FREECAD ASSEMBLY — COMPONENT RECIPES ("LPHolderAssembly")

This assembly document has 2 components, labeled P0..P1 below (a component is one placed body or linked part). 1 of them carries a construction recipe — the FreeCAD feature program that regenerates the part from scratch, quoted from this document or its linked companion documents; the rest are supplied as boundary geometry only. No exploded tour is included for this assembly.
COMPONENT P0 — geometry summary ("Body001"; no construction recipe available for this part):
  bounding box: 159.3 x 92.6 x 7.3 mm
  tessellated surface: 30,212 triangles
  volume: 10545 mm^3 (10% of its bounding box)
  symmetry: mirror-symmetric across its y mid-plane
COMPONENT P1 — recipe-attached ("Record Case", a linked part whose construction recipe lives in a companion FreeCAD document of the same project; that document's serialized recipe follows).
Construction recipe (the companion document, serialized — sketch geometry with constraints, then the solid features built on it; lengths are millimeters unless a unit is written):

FCSTD DOCUMENT  (FreeCAD 1.2R20251216 (Git shallow))
Label: Record
License: All rights reserved
objects: Sketcher::SketchObject×2, PartDesign::Pad×2, App::Point×1, PartDesign::Body×1
note: 11 computed .brp shape members not serialized (recipe doc carries the construction recipe); baked Part::Feature solids carry a one-line shape summary decoded from their .brp

FEATURE [App::Point] Origin001
  Role = Origin
FEATURE [Sketcher::SketchObject] Sketch
  ArcFitTolerance = 1e-06
  AttachmentSupport = -> [Origin]
  ExternalTypes = [0]
  FullyConstrained = false
  MakeInternals = false
  MapMode = 5
  Placement = pos=(0,0,0) rot=(1,0,0;1.5708rad)
  sketch-geometry (5):
    g0: LineSegment StartX=-151.615 StartY=152.4 StartZ=0 EndX=-151.615 EndY=-152.4 EndZ=0
    g1: LineSegment StartX=-151.615 StartY=-152.4 StartZ=0 EndX=153.185 EndY=-152.4 EndZ=0
    g2: LineSegment StartX=153.185 StartY=-152.4 StartZ=0 EndX=153.185 EndY=152.4 EndZ=0
    g3: LineSegment StartX=153.185 StartY=152.4 StartZ=0 EndX=-151.615 EndY=152.4 EndZ=0
    g4: GeomPoint [constr] X=0.784725 Y=3.6e-15 Z=0
  constraints (12):
    c: Coincident(g0,g1)
    c: Coincident(g1,g2)
    c: Coincident(g2,g3)
    c: Coincident(g3,g0)
    c: Vertical(g0)
    c: Vertical(g2)
    c: Horizontal(g1)
    c: Horizontal(g3)
    c: Symmetric(g2,g0,g4)
    c: DistanceX(g3,g3) = 304.8
    c: DistanceY(g0,g0) = 304.8
    c: Distance(g-1,g3) = 152.4
FEATURE [PartDesign::Pad] Pad
  Direction = (0,-1,2e-16)
  Length = 0.254
  Length2 = 10
  Profile = -> Sketch
  ReferenceAxis = -> Sketch [N_Axis]
  Refine = true
  SideType = 0
  Suppressed = false
  Type = 0
  Type2 = 0
FEATURE [Sketcher::SketchObject] Sketch001
  ArcFitTolerance = 1e-06
  AttachmentSupport = -> [Origin]
  ExternalTypes = [0]
  FullyConstrained = true
  MakeInternals = false
  MapMode = 5
  Placement = pos=(0,0,0) rot=(1,0,0;1.5708rad)
  sketch-geometry (1):
    g0: Circle CenterX=0 CenterY=0 CenterZ=0 NormalX=0 NormalY=0 NormalZ=1 AngleXU=0 Radius=82.55
  constraints (2):
    c: Coincident(g0,g-1)
    c: Diameter(g0) = 165.1
FEATURE [PartDesign::Pad] Pad001  label="Center circle"
  BaseFeature = -> Pad
  Direction = (0,-1,0)
  Length = 9.906
  Length2 = 10
  Profile = -> Sketch001
  ReferenceAxis = -> Sketch001 [N_Axis]
  Refine = true
  SideType = 0
  Suppressed = false
  Type = 0
  Type2 = 0
FEATURE [PartDesign::Body] Body  label="Record Case"
  AllowCompound = true
  Group = -> [Sketch,Pad,Sketch001,Pad001]
  Origin = -> Origin
  Tip = -> Pad001
PROVENANCE & LICENSES
A FreeCAD (.FCStd) document from a public repository crawl; recipes are the document's own serialized feature recipes (and, for linked parts, companion documents' recipes).
License: as declared in the source repository (recorded in the dataset sidecar).
